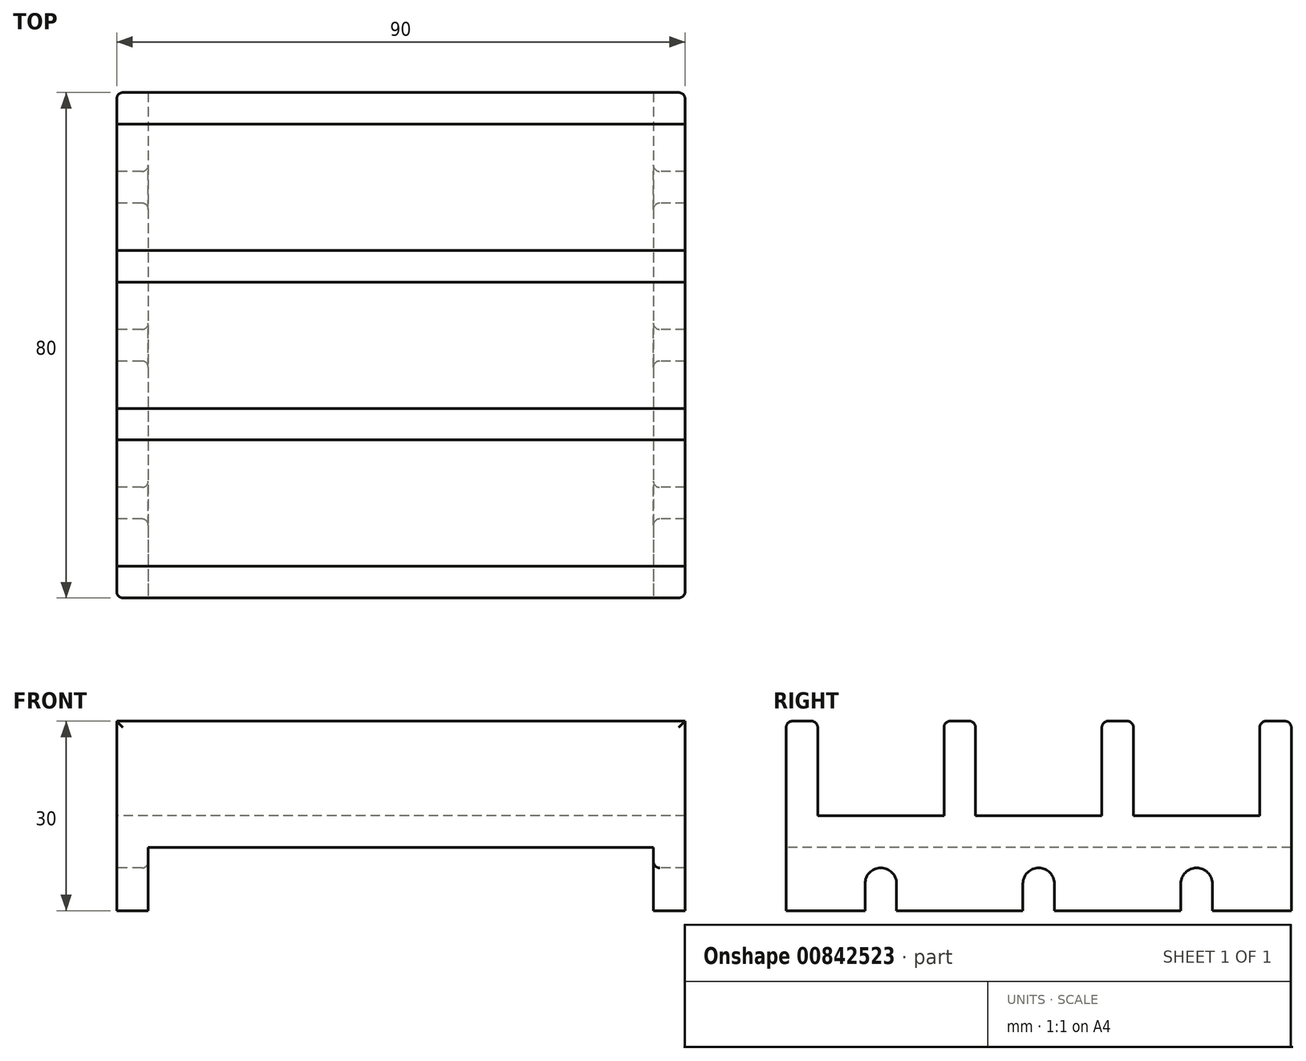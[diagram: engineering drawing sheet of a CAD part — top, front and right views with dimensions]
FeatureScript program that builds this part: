
annotation { "Feature Type Name" : "Feature", "Feature Type Description" : "" }
export const myFeature = defineFeature(function(context is Context, id is Id, definition is map)
    precondition{}
    {
        {
            var Q0;
            Q0=qCreatedBy(makeId("Right.planeOp"),FACE);
            var sketch = newSketch(context, id + "F0", { "sketchPlane" : qUnion([Q0])});
            skLineSegment(sketch, "E0.bottom", {"start": v(-2.5, 0) * mm, "end": v(77.5, 0) * mm});
            skLineSegment(sketch, "E0.top", {"start": v(-2.5, 30) * mm, "end": v(77.5, 30) * mm});
            skLineSegment(sketch, "E0.left", {"start": v(-2.5, 0) * mm, "end": v(-2.5, 30) * mm});
            skLineSegment(sketch, "E0.right", {"start": v(77.5, 0) * mm, "end": v(77.5, 30) * mm});
            skLineSegment(sketch, "E1", {"start": v(0, 0) * mm, "end": v(-2.5, 0) * mm});
            skSolve(sketch);
        }
        {
            var Q0;
            Q0=makeQuery(id+"F0.imprint","IMPRINT",FACE,{"disambiguationData":[TD([[makeQuery(id+"F0.imprint","IMPRINT",EDGE,{"derivedFrom":sQuery(id+"F0.wireOp",EDGE,"E0.bottom")}),1.0]])]});
            extrude(context, id + "F1", {"entities" : qUnion([Q0]), "depth" : 90 * mm, "offsetDistance" : 25 * mm});
        }
        {
            var Q0;
            Q0=qCreatedBy(makeId("Right.planeOp"),FACE);
            var sketch = newSketch(context, id + "F2", { "sketchPlane" : qUnion([Q0])});
            skCircle(sketch, "E2", {"center": v(12.5, 4.26) * mm, "radius": 2.5 * mm});
            skLineSegment(sketch, "E3", {"start": v(10, 4.26) * mm, "end": v(10, 0) * mm});
            skLineSegment(sketch, "E4", {"start": v(15, 4.26) * mm, "end": v(15, 0) * mm});
            skLineSegment(sketch, "E5", {"start": v(10, 0) * mm, "end": v(15, 0) * mm});
            skCircle(sketch, "E6.1.0.0", {"center": v(37.5, 4.26) * mm, "radius": 2.5 * mm});
            skLineSegment(sketch, "E6.1.0.1", {"start": v(35, 0) * mm, "end": v(40, 0) * mm});
            skLineSegment(sketch, "E6.1.0.2", {"start": v(35, 4.26) * mm, "end": v(35, 0) * mm});
            skLineSegment(sketch, "E6.1.0.3", {"start": v(40, 4.26) * mm, "end": v(40, 0) * mm});
            skCircle(sketch, "E6.2.0.0", {"center": v(62.5, 4.26) * mm, "radius": 2.5 * mm});
            skLineSegment(sketch, "E6.2.0.1", {"start": v(60, 0) * mm, "end": v(65, 0) * mm});
            skLineSegment(sketch, "E6.2.0.2", {"start": v(60, 4.26) * mm, "end": v(60, 0) * mm});
            skLineSegment(sketch, "E6.2.0.3", {"start": v(65, 4.26) * mm, "end": v(65, 0) * mm});
            skLineSegment(sketch, "E6.direction1", {"start": v(10, 0) * mm, "end": v(35, 0) * mm, "construction": true});
            skLineSegment(sketch, "E7", {"start": v(0, 0) * mm, "end": v(10, 0) * mm});
            skSolve(sketch);
        }
        {
            var Q0;
            Q0 = qSketchRegion(id + "F2", true);
            extrude(context, id + "F3", {"entities" : qUnion([Q0]), "operationType" : NewBodyOperationType.REMOVE, "depth" : 90 * mm, "offsetDistance" : 25 * mm});
        }
        {
            var Q0;
            Q0=qCreatedBy(makeId("Right.planeOp"),FACE);
            var sketch = newSketch(context, id + "F4", { "sketchPlane" : qUnion([Q0])});
            skLineSegment(sketch, "E8.bottom", {"start": v(2.5, 15) * mm, "end": v(22.5, 15) * mm});
            skLineSegment(sketch, "E8.top", {"start": v(2.5, 45) * mm, "end": v(22.5, 45) * mm});
            skLineSegment(sketch, "E8.left", {"start": v(2.5, 15) * mm, "end": v(2.5, 45) * mm});
            skLineSegment(sketch, "E8.right", {"start": v(22.5, 15) * mm, "end": v(22.5, 45) * mm});
            skLineSegment(sketch, "E9.1.0.0", {"start": v(27.5, 45) * mm, "end": v(47.5, 45) * mm});
            skLineSegment(sketch, "E9.1.0.1", {"start": v(27.5, 15) * mm, "end": v(47.5, 15) * mm});
            skLineSegment(sketch, "E9.1.0.2", {"start": v(47.5, 15) * mm, "end": v(47.5, 45) * mm});
            skLineSegment(sketch, "E9.1.0.3", {"start": v(27.5, 15) * mm, "end": v(27.5, 45) * mm});
            skLineSegment(sketch, "E9.2.0.0", {"start": v(52.5, 45) * mm, "end": v(72.5, 45) * mm});
            skLineSegment(sketch, "E9.2.0.1", {"start": v(52.5, 15) * mm, "end": v(72.5, 15) * mm});
            skLineSegment(sketch, "E9.2.0.2", {"start": v(72.5, 15) * mm, "end": v(72.5, 45) * mm});
            skLineSegment(sketch, "E9.2.0.3", {"start": v(52.5, 15) * mm, "end": v(52.5, 45) * mm});
            skLineSegment(sketch, "E9.direction1", {"start": v(2.5, 15) * mm, "end": v(27.5, 15) * mm, "construction": true});
            skLineSegment(sketch, "E10", {"start": v(52.5, 15) * mm, "end": v(52.5, 0) * mm});
            skSolve(sketch);
        }
        {
            var Q0;
            Q0=makeQuery(id+"F4.imprint","IMPRINT",FACE,{"disambiguationData":[TD([[makeQuery(id+"F4.imprint","IMPRINT",EDGE,{"derivedFrom":sQuery(id+"F4.wireOp",EDGE,"E8.bottom")}),1.0]])]});
            var Q1;
            Q1=makeQuery(id+"F4.imprint","IMPRINT",FACE,{"disambiguationData":[TD([[makeQuery(id+"F4.imprint","IMPRINT",EDGE,{"derivedFrom":sQuery(id+"F4.wireOp",EDGE,"E9.1.0.0")}),-1.0]])]});
            var Q2;
            Q2=makeQuery(id+"F4.imprint","IMPRINT",FACE,{"disambiguationData":[TD([[makeQuery(id+"F4.imprint","IMPRINT",EDGE,{"derivedFrom":sQuery(id+"F4.wireOp",EDGE,"E9.2.0.0")}),-1.0]])]});
            var Q3;
            Q3 = qConstructionFilter(qBodyType(qCreatedBy(id + "F4" ,EDGE), BodyType.WIRE), ConstructionObject.NO);
            extrude(context, id + "F5", {"entities" : qUnion([Q0, Q1, Q2]), "operationType" : NewBodyOperationType.REMOVE, "surfaceEntities" : qUnion([Q3]), "depth" : 90 * mm, "offsetDistance" : 25 * mm});
        }
        {
            var Q0;
            Q0=makeQuery(id+"F1.opExtrude","SWEPT_FACE",FACE,{"disambiguationData":[OSD([sQuery(id+"F0.wireOp",EDGE,"E0.left")])]});
            var sketch = newSketch(context, id + "F6", { "sketchPlane" : qUnion([Q0])});
            skLineSegment(sketch, "E11.bottom", {"start": v(5, 10) * mm, "end": v(85, 10) * mm});
            skLineSegment(sketch, "E11.top", {"start": v(5, 0) * mm, "end": v(85, 0) * mm});
            skLineSegment(sketch, "E11.left", {"start": v(5, 10) * mm, "end": v(5, 0) * mm});
            skLineSegment(sketch, "E11.right", {"start": v(85, 10) * mm, "end": v(85, 0) * mm});
            skLineSegment(sketch, "E12", {"start": v(0, 0) * mm, "end": v(5, 0) * mm});
            skLineSegment(sketch, "E13", {"start": v(85, 0) * mm, "end": v(90, 0) * mm});
            skSolve(sketch);
        }
        {
            var Q0;
            Q0=makeQuery(id+"F6.imprint","IMPRINT",FACE,{"disambiguationData":[TD([[makeQuery(id+"F6.imprint","IMPRINT",EDGE,{"derivedFrom":sQuery(id+"F6.wireOp",EDGE,"E11.bottom")}),-1.0]])]});
            extrude(context, id + "F7", {"entities" : qUnion([Q0]), "operationType" : NewBodyOperationType.REMOVE, "depth" : -90 * mm, "offsetDistance" : 25 * mm});
        }
        {
            var Q0;
            Q0=makeQuery(id+"F1.opExtrude","SWEPT_EDGE",EDGE,{"disambiguationData":[OSD([sQuery(id+"F0.wireOp",EDGE,"E0.top"),sQuery(id+"F0.wireOp",EDGE,"E0.left")])]});
            var Q1;
            Q1=makeQuery(id+"F5.boolean.opBoolean","INTERSECT",EDGE,{"derivedFrom":[makeQuery(id+"F1.opExtrude","SWEPT_FACE",FACE,{"disambiguationData":[OSD([sQuery(id+"F0.wireOp",EDGE,"E0.top")])]}),makeQuery(id+"F5.opExtrude","SWEPT_FACE",FACE,{"disambiguationData":[OSD([sQuery(id+"F4.wireOp",EDGE,"E8.right")])]})]});
            var Q2;
            Q2=makeQuery(id+"F5.boolean.opBoolean","INTERSECT",EDGE,{"derivedFrom":[makeQuery(id+"F1.opExtrude","SWEPT_FACE",FACE,{"disambiguationData":[OSD([sQuery(id+"F0.wireOp",EDGE,"E0.top")])]}),makeQuery(id+"F5.opExtrude","SWEPT_FACE",FACE,{"disambiguationData":[OSD([sQuery(id+"F4.wireOp",EDGE,"E9.1.0.2")])]})]});
            var Q3;
            Q3=makeQuery(id+"F5.boolean.opBoolean","INTERSECT",EDGE,{"derivedFrom":[makeQuery(id+"F1.opExtrude","SWEPT_FACE",FACE,{"disambiguationData":[OSD([sQuery(id+"F0.wireOp",EDGE,"E0.top")])]}),makeQuery(id+"F5.opExtrude","SWEPT_FACE",FACE,{"disambiguationData":[OSD([sQuery(id+"F4.wireOp",EDGE,"E9.2.0.2")])]})]});
            var Q4;
            Q4=makeQuery(id+"F5.boolean.opBoolean","INTERSECT",EDGE,{"derivedFrom":[makeQuery(id+"F1.opExtrude","SWEPT_FACE",FACE,{"disambiguationData":[OSD([sQuery(id+"F0.wireOp",EDGE,"E0.top")])]}),makeQuery(id+"F5.opExtrude","SWEPT_FACE",FACE,{"disambiguationData":[OSD([sQuery(id+"F4.wireOp",EDGE,"E9.1.0.3")])]})]});
            var Q5;
            Q5=makeQuery(id+"F5.boolean.opBoolean","INTERSECT",EDGE,{"derivedFrom":[makeQuery(id+"F1.opExtrude","SWEPT_FACE",FACE,{"disambiguationData":[OSD([sQuery(id+"F0.wireOp",EDGE,"E0.top")])]}),makeQuery(id+"F5.opExtrude","SWEPT_FACE",FACE,{"disambiguationData":[OSD([sQuery(id+"F4.wireOp",EDGE,"E9.2.0.3")])]})]});
            var Q6;
            Q6=makeQuery(id+"F5.boolean.opBoolean","COPY",EDGE,{"derivedFrom":makeQuery(id+"F5.opExtrude","CAP_EDGE",EDGE,{"disambiguationData":[OSD([sQuery(id+"F4.wireOp",EDGE,"E8.bottom")])],"isStart":false})});
            var Q7;
            Q7=makeQuery(id+"F5.boolean.opBoolean","COPY",EDGE,{"derivedFrom":makeQuery(id+"F5.opExtrude","CAP_EDGE",EDGE,{"disambiguationData":[OSD([sQuery(id+"F4.wireOp",EDGE,"E9.1.0.1")])],"isStart":false})});
            var Q8;
            Q8=makeQuery(id+"F5.boolean.opBoolean","COPY",EDGE,{"derivedFrom":makeQuery(id+"F5.opExtrude","CAP_EDGE",EDGE,{"disambiguationData":[OSD([sQuery(id+"F4.wireOp",EDGE,"E9.2.0.1")])],"isStart":false})});
            var Q9;
            Q9=makeQuery(id+"F1.opExtrude","CAP_EDGE",EDGE,{"disambiguationData":[OSD([sQuery(id+"F0.wireOp",EDGE,"E0.left")])],"isStart":false});
            var Q10;
            Q10=makeQuery(id+"F1.opExtrude","CAP_EDGE",EDGE,{"disambiguationData":[OSD([sQuery(id+"F0.wireOp",EDGE,"E0.left")])],"isStart":true});
            var Q11;
            Q11=makeQuery(id+"F7.boolean.opBoolean","COPY",EDGE,{"derivedFrom":makeQuery(id+"F7.opExtrude","CAP_EDGE",EDGE,{"disambiguationData":[OSD([sQuery(id+"F6.wireOp",EDGE,"E11.bottom")])],"isStart":true})});
            var Q12;
            Q12=makeQuery(id+"F7.boolean.opBoolean","INTERSECT",EDGE,{"derivedFrom":[makeQuery(id+"F5.boolean.opBoolean","COPY",FACE,{"derivedFrom":makeQuery(id+"F5.opExtrude","SWEPT_FACE",FACE,{"disambiguationData":[OSD([sQuery(id+"F4.wireOp",EDGE,"E8.left")])]})}),makeQuery(id+"F7.opExtrude","SWEPT_FACE",FACE,{"disambiguationData":[OSD([sQuery(id+"F6.wireOp",EDGE,"E11.bottom")])]})]});
            var Q13;
            Q13=makeQuery(id+"F7.boolean.opBoolean","INTERSECT",EDGE,{"derivedFrom":[makeQuery(id+"F5.boolean.opBoolean","COPY",FACE,{"derivedFrom":makeQuery(id+"F5.opExtrude","SWEPT_FACE",FACE,{"disambiguationData":[OSD([sQuery(id+"F4.wireOp",EDGE,"E8.right")])]})}),makeQuery(id+"F7.opExtrude","SWEPT_FACE",FACE,{"disambiguationData":[OSD([sQuery(id+"F6.wireOp",EDGE,"E11.bottom")])]})]});
            var Q14;
            Q14=makeQuery(id+"F7.boolean.opBoolean","INTERSECT",EDGE,{"derivedFrom":[makeQuery(id+"F5.boolean.opBoolean","COPY",FACE,{"derivedFrom":makeQuery(id+"F5.opExtrude","SWEPT_FACE",FACE,{"disambiguationData":[OSD([sQuery(id+"F4.wireOp",EDGE,"E9.1.0.3")])]})}),makeQuery(id+"F7.opExtrude","SWEPT_FACE",FACE,{"disambiguationData":[OSD([sQuery(id+"F6.wireOp",EDGE,"E11.bottom")])]})]});
            var Q15;
            Q15=makeQuery(id+"F7.boolean.opBoolean","INTERSECT",EDGE,{"derivedFrom":[makeQuery(id+"F5.boolean.opBoolean","COPY",FACE,{"derivedFrom":makeQuery(id+"F5.opExtrude","SWEPT_FACE",FACE,{"disambiguationData":[OSD([sQuery(id+"F4.wireOp",EDGE,"E9.1.0.2")])]})}),makeQuery(id+"F7.opExtrude","SWEPT_FACE",FACE,{"disambiguationData":[OSD([sQuery(id+"F6.wireOp",EDGE,"E11.bottom")])]})]});
            var Q16;
            Q16=makeQuery(id+"F7.boolean.opBoolean","INTERSECT",EDGE,{"derivedFrom":[makeQuery(id+"F5.boolean.opBoolean","COPY",FACE,{"derivedFrom":makeQuery(id+"F5.opExtrude","SWEPT_FACE",FACE,{"disambiguationData":[OSD([sQuery(id+"F4.wireOp",EDGE,"E9.2.0.3")])]})}),makeQuery(id+"F7.opExtrude","SWEPT_FACE",FACE,{"disambiguationData":[OSD([sQuery(id+"F6.wireOp",EDGE,"E11.bottom")])]})]});
            var Q17;
            Q17=makeQuery(id+"F7.boolean.opBoolean","INTERSECT",EDGE,{"derivedFrom":[makeQuery(id+"F5.boolean.opBoolean","COPY",FACE,{"derivedFrom":makeQuery(id+"F5.opExtrude","SWEPT_FACE",FACE,{"disambiguationData":[OSD([sQuery(id+"F4.wireOp",EDGE,"E9.2.0.2")])]})}),makeQuery(id+"F7.opExtrude","SWEPT_FACE",FACE,{"disambiguationData":[OSD([sQuery(id+"F6.wireOp",EDGE,"E11.bottom")])]})]});
            var Q18;
            Q18=makeQuery(id+"F1.opExtrude","SWEPT_EDGE",EDGE,{"disambiguationData":[OSD([sQuery(id+"F0.wireOp",EDGE,"E0.top"),sQuery(id+"F0.wireOp",EDGE,"E0.right")])]});
            var Q19;
            Q19=makeQuery(id+"F7.boolean.opBoolean","COPY",EDGE,{"derivedFrom":makeQuery(id+"F7.opExtrude","CAP_EDGE",EDGE,{"disambiguationData":[OSD([sQuery(id+"F6.wireOp",EDGE,"E11.bottom")])],"isStart":false})});
            var Q20;
            Q20=makeQuery(id+"F7.boolean.opBoolean","COPY",EDGE,{"derivedFrom":makeQuery(id+"F7.opExtrude","CAP_EDGE",EDGE,{"disambiguationData":[OSD([sQuery(id+"F6.wireOp",EDGE,"E11.left")])],"isStart":true})});
            var Q21;
            Q21=makeQuery(id+"F7.boolean.opBoolean","COPY",EDGE,{"derivedFrom":makeQuery(id+"F7.opExtrude","CAP_EDGE",EDGE,{"disambiguationData":[OSD([sQuery(id+"F6.wireOp",EDGE,"E11.right")])],"isStart":true})});
            var Q22;
            Q22=makeQuery(id+"F7.boolean.opBoolean","INTERSECT",EDGE,{"derivedFrom":[makeQuery(id+"F3.boolean.opBoolean","COPY",FACE,{"derivedFrom":makeQuery(id+"F3.opExtrude","SWEPT_FACE",FACE,{"disambiguationData":[OSD([sQuery(id+"F2.wireOp",EDGE,"E4")])]})}),makeQuery(id+"F7.opExtrude","SWEPT_FACE",FACE,{"disambiguationData":[OSD([sQuery(id+"F6.wireOp",EDGE,"E11.right")])]})]});
            var Q23;
            Q23=makeQuery(id+"F7.boolean.opBoolean","INTERSECT",EDGE,{"derivedFrom":[makeQuery(id+"F3.boolean.opBoolean","COPY",FACE,{"derivedFrom":makeQuery(id+"F3.opExtrude","SWEPT_FACE",FACE,{"disambiguationData":[OSD([sQuery(id+"F2.wireOp",EDGE,"E6.1.0.2")])]})}),makeQuery(id+"F7.opExtrude","SWEPT_FACE",FACE,{"disambiguationData":[OSD([sQuery(id+"F6.wireOp",EDGE,"E11.right")])]})]});
            var Q24;
            Q24=makeQuery(id+"F7.boolean.opBoolean","INTERSECT",EDGE,{"derivedFrom":[makeQuery(id+"F3.boolean.opBoolean","COPY",FACE,{"derivedFrom":makeQuery(id+"F3.opExtrude","SWEPT_FACE",FACE,{"disambiguationData":[OSD([sQuery(id+"F2.wireOp",EDGE,"E6.2.0.2")])]})}),makeQuery(id+"F7.opExtrude","SWEPT_FACE",FACE,{"disambiguationData":[OSD([sQuery(id+"F6.wireOp",EDGE,"E11.right")])]})]});
            var Q25;
            Q25=makeQuery(id+"F7.boolean.opBoolean","INTERSECT",EDGE,{"derivedFrom":[makeQuery(id+"F3.boolean.opBoolean","COPY",FACE,{"derivedFrom":makeQuery(id+"F3.opExtrude","SWEPT_FACE",FACE,{"disambiguationData":[OSD([sQuery(id+"F2.wireOp",EDGE,"E4")])]})}),makeQuery(id+"F7.opExtrude","SWEPT_FACE",FACE,{"disambiguationData":[OSD([sQuery(id+"F6.wireOp",EDGE,"E11.left")])]})]});
            var Q26;
            Q26=makeQuery(id+"F7.boolean.opBoolean","INTERSECT",EDGE,{"derivedFrom":[makeQuery(id+"F3.boolean.opBoolean","COPY",FACE,{"derivedFrom":makeQuery(id+"F3.opExtrude","SWEPT_FACE",FACE,{"disambiguationData":[OSD([sQuery(id+"F2.wireOp",EDGE,"E6.1.0.2")])]})}),makeQuery(id+"F7.opExtrude","SWEPT_FACE",FACE,{"disambiguationData":[OSD([sQuery(id+"F6.wireOp",EDGE,"E11.left")])]})]});
            var Q27;
            Q27=makeQuery(id+"F7.boolean.opBoolean","INTERSECT",EDGE,{"derivedFrom":[makeQuery(id+"F3.boolean.opBoolean","COPY",FACE,{"derivedFrom":makeQuery(id+"F3.opExtrude","SWEPT_FACE",FACE,{"disambiguationData":[OSD([sQuery(id+"F2.wireOp",EDGE,"E6.2.0.2")])]})}),makeQuery(id+"F7.opExtrude","SWEPT_FACE",FACE,{"disambiguationData":[OSD([sQuery(id+"F6.wireOp",EDGE,"E11.left")])]})]});
            var Q28;
            Q28=makeQuery(id+"F1.opExtrude","CAP_EDGE",EDGE,{"disambiguationData":[OSD([sQuery(id+"F0.wireOp",EDGE,"E0.right")])],"isStart":false});
            var Q29;
            Q29=makeQuery(id+"F7.boolean.opBoolean","COPY",EDGE,{"derivedFrom":makeQuery(id+"F7.opExtrude","CAP_EDGE",EDGE,{"disambiguationData":[OSD([sQuery(id+"F6.wireOp",EDGE,"E11.right")])],"isStart":false})});
            var Q30;
            Q30=makeQuery(id+"F7.boolean.opBoolean","COPY",EDGE,{"derivedFrom":makeQuery(id+"F7.opExtrude","CAP_EDGE",EDGE,{"disambiguationData":[OSD([sQuery(id+"F6.wireOp",EDGE,"E11.left")])],"isStart":false})});
            var Q31;
            Q31=makeQuery(id+"F1.opExtrude","CAP_EDGE",EDGE,{"disambiguationData":[OSD([sQuery(id+"F0.wireOp",EDGE,"E0.right")])],"isStart":true});
            var Q32;
            Q32=makeQuery(id+"F5.boolean.opBoolean","COPY",EDGE,{"derivedFrom":makeQuery(id+"F5.opExtrude","CAP_EDGE",EDGE,{"disambiguationData":[OSD([sQuery(id+"F4.wireOp",EDGE,"E8.right")])],"isStart":true})});
            var Q33;
            Q33=makeQuery(id+"F5.boolean.opBoolean","COPY",EDGE,{"derivedFrom":makeQuery(id+"F5.opExtrude","CAP_EDGE",EDGE,{"disambiguationData":[OSD([sQuery(id+"F4.wireOp",EDGE,"E9.1.0.3")])],"isStart":true})});
            var Q34;
            Q34=makeQuery(id+"F5.boolean.opBoolean","COPY",EDGE,{"derivedFrom":makeQuery(id+"F5.opExtrude","CAP_EDGE",EDGE,{"disambiguationData":[OSD([sQuery(id+"F4.wireOp",EDGE,"E9.1.0.2")])],"isStart":true})});
            var Q35;
            Q35=makeQuery(id+"F5.boolean.opBoolean","COPY",EDGE,{"derivedFrom":makeQuery(id+"F5.opExtrude","CAP_EDGE",EDGE,{"disambiguationData":[OSD([sQuery(id+"F4.wireOp",EDGE,"E9.2.0.3")])],"isStart":true})});
            var Q36;
            Q36=makeQuery(id+"F5.boolean.opBoolean","COPY",EDGE,{"derivedFrom":makeQuery(id+"F5.opExtrude","CAP_EDGE",EDGE,{"disambiguationData":[OSD([sQuery(id+"F4.wireOp",EDGE,"E8.left")])],"isStart":true})});
            var Q37;
            Q37=makeQuery(id+"F5.boolean.opBoolean","COPY",EDGE,{"derivedFrom":makeQuery(id+"F5.opExtrude","CAP_EDGE",EDGE,{"disambiguationData":[OSD([sQuery(id+"F4.wireOp",EDGE,"E9.1.0.3")])],"isStart":false})});
            var Q38;
            Q38=makeQuery(id+"F5.boolean.opBoolean","COPY",EDGE,{"derivedFrom":makeQuery(id+"F5.opExtrude","CAP_EDGE",EDGE,{"disambiguationData":[OSD([sQuery(id+"F4.wireOp",EDGE,"E8.right")])],"isStart":false})});
            var Q39;
            Q39=makeQuery(id+"F5.boolean.opBoolean","COPY",EDGE,{"derivedFrom":makeQuery(id+"F5.opExtrude","CAP_EDGE",EDGE,{"disambiguationData":[OSD([sQuery(id+"F4.wireOp",EDGE,"E8.left")])],"isStart":false})});
            var Q40;
            Q40=makeQuery(id+"F5.boolean.opBoolean","COPY",EDGE,{"derivedFrom":makeQuery(id+"F5.opExtrude","CAP_EDGE",EDGE,{"disambiguationData":[OSD([sQuery(id+"F4.wireOp",EDGE,"E9.1.0.2")])],"isStart":false})});
            var Q41;
            Q41=makeQuery(id+"F5.boolean.opBoolean","COPY",EDGE,{"derivedFrom":makeQuery(id+"F5.opExtrude","CAP_EDGE",EDGE,{"disambiguationData":[OSD([sQuery(id+"F4.wireOp",EDGE,"E9.2.0.3")])],"isStart":false})});
            var Q42;
            Q42=makeQuery(id+"F5.boolean.opBoolean","COPY",EDGE,{"derivedFrom":makeQuery(id+"F5.opExtrude","CAP_EDGE",EDGE,{"disambiguationData":[OSD([sQuery(id+"F4.wireOp",EDGE,"E9.2.0.2")])],"isStart":false})});
            var Q43;
            Q43=makeQuery(id+"F5.boolean.opBoolean","INTERSECT",EDGE,{"derivedFrom":[makeQuery(id+"F1.opExtrude","SWEPT_FACE",FACE,{"disambiguationData":[OSD([sQuery(id+"F0.wireOp",EDGE,"E0.top")])]}),makeQuery(id+"F5.opExtrude","SWEPT_FACE",FACE,{"disambiguationData":[OSD([sQuery(id+"F4.wireOp",EDGE,"E8.left")])]})]});
            var Q44;
            Q44=makeQuery(id+"F3.boolean.opBoolean","COPY",EDGE,{"derivedFrom":makeQuery(id+"F3.opExtrude","CAP_EDGE",EDGE,{"disambiguationData":[OSD([sQuery(id+"F2.wireOp",EDGE,"E4")])],"isStart":false})});
            var Q45;
            Q45=makeQuery(id+"F3.boolean.opBoolean","COPY",EDGE,{"derivedFrom":makeQuery(id+"F3.opExtrude","CAP_EDGE",EDGE,{"disambiguationData":[OSD([sQuery(id+"F2.wireOp",EDGE,"E6.1.0.3")])],"isStart":false})});
            var Q46;
            Q46=makeQuery(id+"F3.boolean.opBoolean","COPY",EDGE,{"derivedFrom":makeQuery(id+"F3.opExtrude","CAP_EDGE",EDGE,{"disambiguationData":[OSD([sQuery(id+"F2.wireOp",EDGE,"E6.2.0.3")])],"isStart":false})});
            var Q47;
            Q47=makeQuery(id+"F3.boolean.opBoolean","COPY",EDGE,{"derivedFrom":makeQuery(id+"F3.opExtrude","CAP_EDGE",EDGE,{"disambiguationData":[OSD([sQuery(id+"F2.wireOp",EDGE,"E6.2.0.3")])],"isStart":true})});
            var Q48;
            Q48=makeQuery(id+"F3.boolean.opBoolean","COPY",EDGE,{"derivedFrom":makeQuery(id+"F3.opExtrude","CAP_EDGE",EDGE,{"disambiguationData":[OSD([sQuery(id+"F2.wireOp",EDGE,"E6.1.0.3")])],"isStart":true})});
            var Q49;
            Q49=makeQuery(id+"F3.boolean.opBoolean","COPY",EDGE,{"derivedFrom":makeQuery(id+"F3.opExtrude","CAP_EDGE",EDGE,{"disambiguationData":[OSD([sQuery(id+"F2.wireOp",EDGE,"E4")])],"isStart":true})});
            var Q50;
            Q50=makeQuery(id+"F5.boolean.opBoolean","COPY",EDGE,{"derivedFrom":makeQuery(id+"F5.opExtrude","CAP_EDGE",EDGE,{"disambiguationData":[OSD([sQuery(id+"F4.wireOp",EDGE,"E8.bottom")])],"isStart":true})});
            var Q51;
            Q51=makeQuery(id+"F5.boolean.opBoolean","COPY",EDGE,{"derivedFrom":makeQuery(id+"F5.opExtrude","CAP_EDGE",EDGE,{"disambiguationData":[OSD([sQuery(id+"F4.wireOp",EDGE,"E9.1.0.1")])],"isStart":true})});
            var Q52;
            Q52=makeQuery(id+"F5.boolean.opBoolean","COPY",EDGE,{"derivedFrom":makeQuery(id+"F5.opExtrude","CAP_EDGE",EDGE,{"disambiguationData":[OSD([sQuery(id+"F4.wireOp",EDGE,"E9.2.0.1")])],"isStart":true})});
            fillet(context, id + "F8", {"entities" : qUnion([Q0, Q1, Q2, Q3, Q4, Q5, Q6, Q7, Q8, Q9, Q10, Q11, Q12, Q13, Q14, Q15, Q16, Q17, Q18, Q19, Q20, Q21, Q22, Q23, Q24, Q25, Q26, Q27, Q28, Q29, Q30, Q31, Q32, Q33, Q34, Q35, Q36, Q37, Q38, Q39, Q40, Q41, Q42, Q43, Q44, Q45, Q46, Q47, Q48, Q49, Q50, Q51, Q52]), "radius" : 1 * mm, "tangentPropagation" : true, "allowEdgeOverflow" : false});
        }
    });
